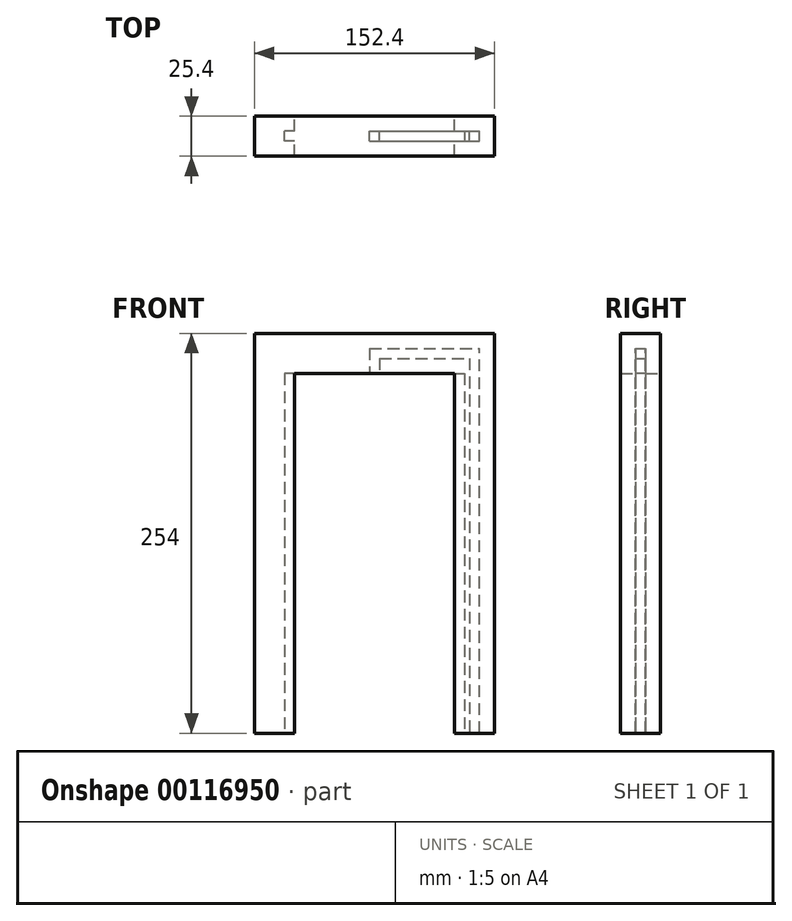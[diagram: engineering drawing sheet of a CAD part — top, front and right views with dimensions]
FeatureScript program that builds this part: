
annotation { "Feature Type Name" : "Feature", "Feature Type Description" : "" }
export const myFeature = defineFeature(function(context is Context, id is Id, definition is map)
    precondition{}
    {
        {
            var Q0;
            Q0=qCreatedBy(makeId("Front.planeOp"),FACE);
            var sketch = newSketch(context, id + "F0", { "sketchPlane" : qUnion([Q0])});
            skLineSegment(sketch, "E0.bottom", {"start": v(76.2, 127) * mm, "end": v(-76.2, 127) * mm});
            skLineSegment(sketch, "E0.top", {"start": v(76.2, -127) * mm, "end": v(-76.2, -127) * mm});
            skLineSegment(sketch, "E0.left", {"start": v(76.2, 127) * mm, "end": v(76.2, -127) * mm});
            skLineSegment(sketch, "E0.right", {"start": v(-76.2, 127) * mm, "end": v(-76.2, -127) * mm});
            skPoint(sketch, "E0.middle", {"position": v(0, 0) * mm});
            skLineSegment(sketch, "E1.bottom", {"start": v(50.8, 101.6) * mm, "end": v(-50.8, 101.6) * mm});
            skLineSegment(sketch, "E1.top", {"start": v(50.8, -101.6) * mm, "end": v(-50.8, -101.6) * mm, "construction": true});
            skLineSegment(sketch, "E1.left", {"start": v(50.8, 101.6) * mm, "end": v(50.8, -101.6) * mm});
            skLineSegment(sketch, "E1.right", {"start": v(-50.8, 101.6) * mm, "end": v(-50.8, -101.6) * mm});
            skLineSegment(sketch, "E2", {"start": v(-50.8, -101.6) * mm, "end": v(-50.8, -127) * mm});
            skLineSegment(sketch, "E3", {"start": v(50.8, -101.6) * mm, "end": v(50.8, -127) * mm});
            skSolve(sketch);
        }
        {
            var Q0;
            Q0=makeQuery(id+"F0.imprint","IMPRINT",FACE,{"disambiguationData":[TD([[makeQuery(id+"F0.imprint","IMPRINT",EDGE,{"derivedFrom":sQuery(id+"F0.wireOp",EDGE,"E0.bottom")}),1.0]])]});
            extrude(context, id + "F1", {"entities" : qUnion([Q0]), "depth" : 25.4 * mm});
        }
        {
            var Q0;
            Q0=makeQuery(id+"F1.opExtrude","SWEPT_FACE",FACE,{"disambiguationData":[OSD([sQuery(id+"F0.wireOp",EDGE,"E1.bottom")])]});
            var sketch = newSketch(context, id + "F2", { "sketchPlane" : qUnion([Q0])});
            skLineSegment(sketch, "E4", {"start": v(0, 0) * mm, "end": v(0, 25.4) * mm, "construction": true});
            skPoint(sketch, "E5", {"position": v(0, 12.7) * mm});
            skLineSegment(sketch, "E6.bottom", {"start": v(-3.18, 15.88) * mm, "end": v(3.17, 15.88) * mm});
            skLineSegment(sketch, "E6.top", {"start": v(-3.18, 9.53) * mm, "end": v(3.17, 9.53) * mm});
            skLineSegment(sketch, "E6.left", {"start": v(-3.18, 15.88) * mm, "end": v(-3.18, 9.53) * mm});
            skLineSegment(sketch, "E6.right", {"start": v(3.17, 15.88) * mm, "end": v(3.17, 9.53) * mm});
            skSolve(sketch);
        }
        {
            var Q0;
            {var subQ0=sQuery(id+"F0.wireOp",EDGE,"E0.top");Q0=makeQuery(id+"F1.opExtrude","SWEPT_FACE",FACE,{"disambiguationData":[OSD([subQ0]),TDD([makeQuery(id+"F0.imprint","IMPRINT",EDGE,{"disambiguationData":[TD([[makeQuery(id+"F0.imprint","INTERSECT",VERTEX,{"derivedFrom":[subQ0,sQuery(id+"F0.wireOp",EDGE,"E0.right")]}),1.0]])],"derivedFrom":subQ0})])]});}
            var sketch = newSketch(context, id + "F3", { "sketchPlane" : qUnion([Q0])});
            skLineSegment(sketch, "E7.bottom", {"start": v(-50.8, 15.88) * mm, "end": v(-57.15, 15.88) * mm});
            skLineSegment(sketch, "E7.top", {"start": v(-50.8, 9.53) * mm, "end": v(-57.15, 9.53) * mm});
            skLineSegment(sketch, "E7.left", {"start": v(-50.8, 15.88) * mm, "end": v(-50.8, 9.53) * mm});
            skLineSegment(sketch, "E7.right", {"start": v(-57.15, 15.88) * mm, "end": v(-57.15, 9.53) * mm});
            skLineSegment(sketch, "E8", {"start": v(-57.15, 15.88) * mm, "end": v(-50.8, 25.4) * mm, "construction": true});
            skLineSegment(sketch, "E9", {"start": v(-57.15, 9.53) * mm, "end": v(-50.8, 0) * mm, "construction": true});
            skLineSegment(sketch, "E10.0", {"start": v(-50.8, 25.4) * mm, "end": v(-76.2, 25.4) * mm, "construction": true});
            skLineSegment(sketch, "E10.1", {"start": v(-76.2, 25.4) * mm, "end": v(-76.2, 0) * mm, "construction": true});
            skLineSegment(sketch, "E10.2", {"start": v(-50.8, 0) * mm, "end": v(-76.2, 0) * mm, "construction": true});
            skLineSegment(sketch, "E11", {"start": v(-63.5, 25.4) * mm, "end": v(-63.5, 0) * mm, "construction": true});
            skLineSegment(sketch, "E12", {"start": v(-57.15, 12.7) * mm, "end": v(-63.5, 12.7) * mm, "construction": true});
            skSolve(sketch);
        }
        {
            var Q0;
            {var subQ0=sQuery(id+"F0.wireOp",EDGE,"E0.top");Q0=makeQuery(id+"F1.opExtrude","SWEPT_FACE",FACE,{"disambiguationData":[OSD([subQ0]),TDD([makeQuery(id+"F0.imprint","IMPRINT",EDGE,{"disambiguationData":[TD([[makeQuery(id+"F0.imprint","INTERSECT",VERTEX,{"derivedFrom":[subQ0,sQuery(id+"F0.wireOp",EDGE,"E0.left")]}),-1.0]])],"derivedFrom":subQ0})])]});}
            var sketch = newSketch(context, id + "F4", { "sketchPlane" : qUnion([Q0])});
            skLineSegment(sketch, "E13.bottom", {"start": v(50.8, 9.53) * mm, "end": v(57.15, 9.53) * mm});
            skLineSegment(sketch, "E13.top", {"start": v(50.8, 15.88) * mm, "end": v(57.15, 15.88) * mm});
            skLineSegment(sketch, "E13.left", {"start": v(50.8, 9.53) * mm, "end": v(50.8, 15.88) * mm});
            skLineSegment(sketch, "E13.right", {"start": v(57.15, 9.53) * mm, "end": v(57.15, 15.88) * mm});
            skLineSegment(sketch, "E14", {"start": v(57.15, 15.88) * mm, "end": v(50.8, 25.4) * mm, "construction": true});
            skLineSegment(sketch, "E15", {"start": v(57.15, 9.53) * mm, "end": v(50.8, 0) * mm, "construction": true});
            skLineSegment(sketch, "E16.0", {"start": v(76.2, 25.4) * mm, "end": v(50.8, 25.4) * mm, "construction": true});
            skLineSegment(sketch, "E16.1", {"start": v(76.2, 25.4) * mm, "end": v(76.2, 0) * mm, "construction": true});
            skLineSegment(sketch, "E16.2", {"start": v(76.2, 0) * mm, "end": v(50.8, 0) * mm, "construction": true});
            skLineSegment(sketch, "E17", {"start": v(63.5, 25.4) * mm, "end": v(63.5, 0) * mm, "construction": true});
            skLineSegment(sketch, "E18", {"start": v(57.15, 12.7) * mm, "end": v(63.5, 12.7) * mm, "construction": true});
            skSolve(sketch);
        }
        {
            var Q0;
            Q0=makeQuery(id+"F3.imprint","IMPRINT",FACE,{"disambiguationData":[TD([[makeQuery(id+"F3.imprint","IMPRINT",EDGE,{"derivedFrom":sQuery(id+"F3.wireOp",EDGE,"E7.bottom")}),1.0]])]});
            var Q1;
            Q1=makeQuery(id+"F4.imprint","IMPRINT",FACE,{"disambiguationData":[TD([[makeQuery(id+"F4.imprint","IMPRINT",EDGE,{"derivedFrom":sQuery(id+"F4.wireOp",EDGE,"E13.bottom")}),1.0]])]});
            extrude(context, id + "F5", {"entities" : qUnion([Q0, Q1]), "operationType" : NewBodyOperationType.REMOVE, "oppositeDirection" : true, "depth" : 228.6 * mm});
        }
        {
            var Q0;
            Q0=qSketchRegion(id+"F2",true);
            extrude(context, id + "F6", {"entities" : qUnion([Q0]), "operationType" : NewBodyOperationType.REMOVE, "oppositeDirection" : true, "depth" : 9.52 * mm});
        }
        {
            var Q0;
            Q0=makeQuery(id+"F1.opExtrude","SWEPT_FACE",FACE,{"disambiguationData":[OSD([sQuery(id+"F0.wireOp",EDGE,"E0.left")])]});
            var sketch = newSketch(context, id + "F7", { "sketchPlane" : qUnion([Q0])});
            skLineSegment(sketch, "E19.0", {"start": v(0, 101.6) * mm, "end": v(-25.4, 101.6) * mm, "construction": true});
            skLineSegment(sketch, "E20", {"start": v(-12.7, 101.6) * mm, "end": v(-12.7, 127) * mm, "construction": true});
            skLineSegment(sketch, "E21.bottom", {"start": v(-15.88, 111.13) * mm, "end": v(-9.53, 111.13) * mm});
            skLineSegment(sketch, "E21.top", {"start": v(-15.88, 117.48) * mm, "end": v(-9.53, 117.48) * mm});
            skLineSegment(sketch, "E21.left", {"start": v(-15.88, 111.13) * mm, "end": v(-15.88, 117.48) * mm});
            skLineSegment(sketch, "E21.right", {"start": v(-9.53, 111.13) * mm, "end": v(-9.53, 117.48) * mm});
            skPoint(sketch, "E21.middle", {"position": v(-12.7, 114.3) * mm});
            skSolve(sketch);
        }
        {
            var Q0;
            Q0=makeQuery(id+"F7.imprint","IMPRINT",FACE,{"disambiguationData":[TD([[makeQuery(id+"F7.imprint","IMPRINT",EDGE,{"derivedFrom":sQuery(id+"F7.wireOp",EDGE,"E21.bottom")}),1.0]])]});
            extrude(context, id + "F8", {"entities" : qUnion([Q0]), "operationType" : NewBodyOperationType.REMOVE, "oppositeDirection" : true, "depth" : 79.38 * mm, "hasSecondDirection" : true, "secondDirectionOppositeDirection" : true, "secondDirectionDepth" : 9.52 * mm});
        }
        {
            var Q0;
            {var subQ6=sQuery(id+"F4.wireOp",EDGE,"E13.bottom");Q0=makeQuery(id+"F4.imprint","IMPRINT",FACE,{"disambiguationData":[TD([[makeQuery(id+"F4.imprint","IMPRINT",EDGE,{"derivedFrom":subQ6}),-1.0]])]});}
            var sketch = newSketch(context, id + "F9", { "sketchPlane" : qUnion([Q0])});
            skPoint(sketch, "E22.0", {"position": v(63.5, 12.7) * mm});
            skLineSegment(sketch, "E23.bottom", {"start": v(60.33, 15.88) * mm, "end": v(66.68, 15.88) * mm});
            skLineSegment(sketch, "E23.top", {"start": v(60.33, 9.53) * mm, "end": v(66.68, 9.53) * mm});
            skLineSegment(sketch, "E23.left", {"start": v(60.33, 15.88) * mm, "end": v(60.33, 9.53) * mm});
            skLineSegment(sketch, "E23.right", {"start": v(66.68, 15.88) * mm, "end": v(66.68, 9.53) * mm});
            skSolve(sketch);
        }
        {
            var Q0;
            Q0=qSketchRegion(id+"F9",true);
            extrude(context, id + "F10", {"entities" : qUnion([Q0]), "operationType" : NewBodyOperationType.REMOVE, "oppositeDirection" : true, "depth" : 238.12 * mm});
        }
    });
